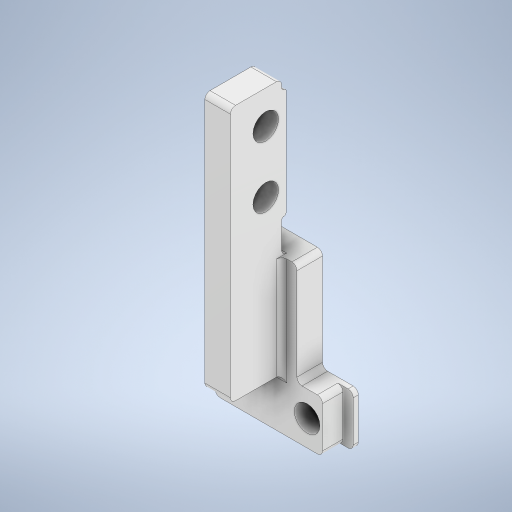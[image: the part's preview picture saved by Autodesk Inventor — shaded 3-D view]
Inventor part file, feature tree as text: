
AUTODESK INVENTOR PART (.ipt)
format: ipt  version: 2024.3 (Build 283343000, 343)  size: 392,704 bytes
history: native  units: mm
features: sketch x6, extrude x5, fillet x3, hole x1, projected_geometry x1
ambient origin geometry x8: Origin, YZ Plane, XZ Plane, XY Plane, X Axis, Y Axis, Z Axis, Center Point
bodies: Body1 (feature_tree)
feature tree (16):
  extrude  "押し出し4"  Depth=5.0mm
  extrude  "押し出し5"  Depth=5.0mm
  hole  "穴3"  [1 undecoded]
  extrude  "押し出し6"  Depth=5.0mm
  fillet  "フィレット4"  Radius=15.0mm
  extrude  "押し出し7"  Depth=5.0mm
  fillet  "フィレット5"  Radius=5.0mm
  extrude  "押し出し8"  Depth=30.0mm
  fillet  "フィレット6"  Radius=5.0mm
  sketch  "スケッチ6"
  sketch  "スケッチ7"
  sketch  "スケッチ8"
  sketch  "スケッチ9"
  sketch  "スケッチ10"
  projected_geometry  "投影ループ1"
  sketch  "スケッチ11"
note: 1 required parameter value undecoded (feature->parameter linkage not recoverable at this tier; creation-order binding heuristic only, values carry confidence <= 0.55)
